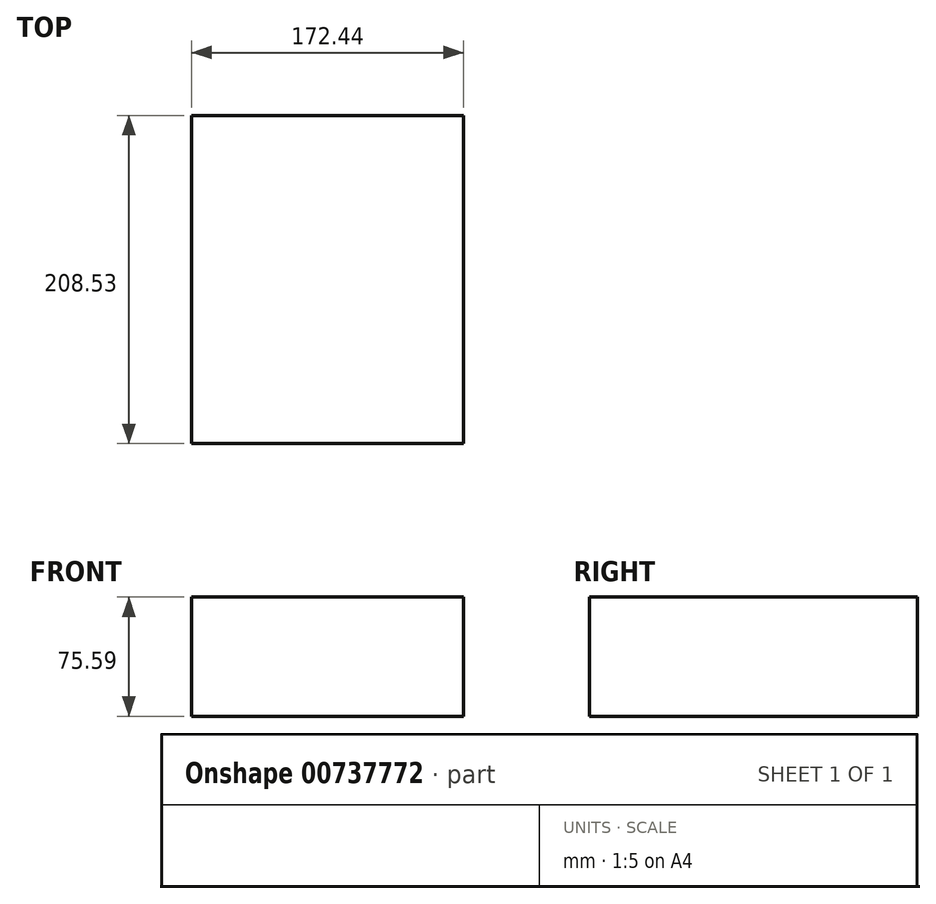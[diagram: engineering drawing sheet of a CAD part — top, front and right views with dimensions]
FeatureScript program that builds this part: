
annotation { "Feature Type Name" : "Feature", "Feature Type Description" : "" }
export const myFeature = defineFeature(function(context is Context, id is Id, definition is map)
    precondition{}
    {
        {
            var Q0;
            Q0=qCreatedBy(makeId("Front.planeOp"),FACE);
            var sketch = newSketch(context, id + "F0", { "sketchPlane" : qUnion([Q0])});
            skLineSegment(sketch, "E0.bottom", {"start": v(0, 0) * mm, "end": v(-75.67, 0) * mm});
            skLineSegment(sketch, "E0.top", {"start": v(0, 75.59) * mm, "end": v(-75.67, 75.59) * mm});
            skLineSegment(sketch, "E0.left", {"start": v(0, 0) * mm, "end": v(0, 75.59) * mm});
            skLineSegment(sketch, "E0.right", {"start": v(-75.67, 0) * mm, "end": v(-75.67, 75.59) * mm});
            skSolve(sketch);
        }
        {
            var Q0;
            Q0=makeQuery(id+"F0.imprint","IMPRINT",FACE,{"disambiguationData":[TD([[makeQuery(id+"F0.imprint","IMPRINT",EDGE,{"derivedFrom":sQuery(id+"F0.wireOp",EDGE,"E0.bottom")}),-1.0]])]});
            extrude(context, id + "F1", {"entities" : qUnion([Q0]), "depth" : 208.53 * mm, "offsetDistance" : 25.4 * mm});
        }
        {
            var Q0;
            Q0=makeQuery(id+"F1.opExtrude","SWEPT_FACE",FACE,{"disambiguationData":[OSD([sQuery(id+"F0.wireOp",EDGE,"E0.right")])]});
            extrude(context, id + "F2", {"entities" : qUnion([Q0]), "operationType" : NewBodyOperationType.ADD, "depth" : 96.77 * mm, "offsetDistance" : 25.4 * mm});
        }
    });
